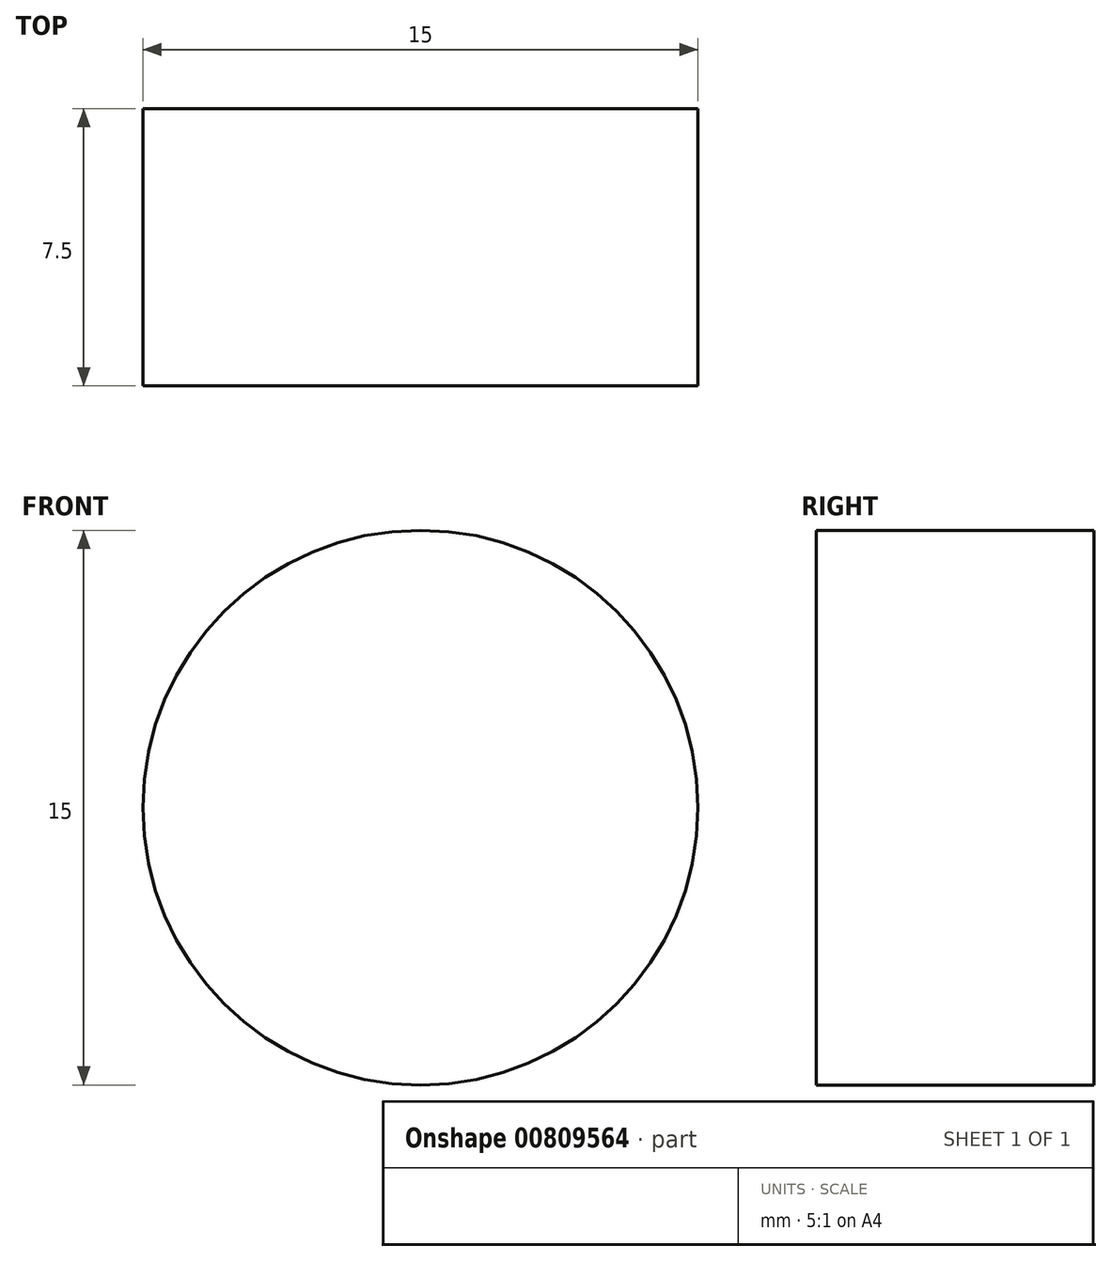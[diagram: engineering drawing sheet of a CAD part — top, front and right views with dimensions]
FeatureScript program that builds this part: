
annotation { "Feature Type Name" : "Feature", "Feature Type Description" : "" }
export const myFeature = defineFeature(function(context is Context, id is Id, definition is map)
    precondition{}
    {
        {
            var Q0;
            Q0=qCreatedBy(makeId("Front.planeOp"),FACE);
            var sketch = newSketch(context, id + "F0", { "sketchPlane" : qUnion([Q0])});
            skCircle(sketch, "E0", {"center": v(0, 0) * mm, "radius": 7.5 * mm});
            skSolve(sketch);
        }
        {
            var Q0;
            Q0=makeQuery(id+"F0.imprint","IMPRINT",FACE,{"disambiguationData":[TD([[makeQuery(id+"F0.imprint","IMPRINT",EDGE,{"derivedFrom":sQuery(id+"F0.wireOp",EDGE,"E0")}),1.0]])]});
            extrude(context, id + "F1", {"entities" : qUnion([Q0]), "depth" : 7.5 * mm, "offsetDistance" : 25.4 * mm});
        }
    });
